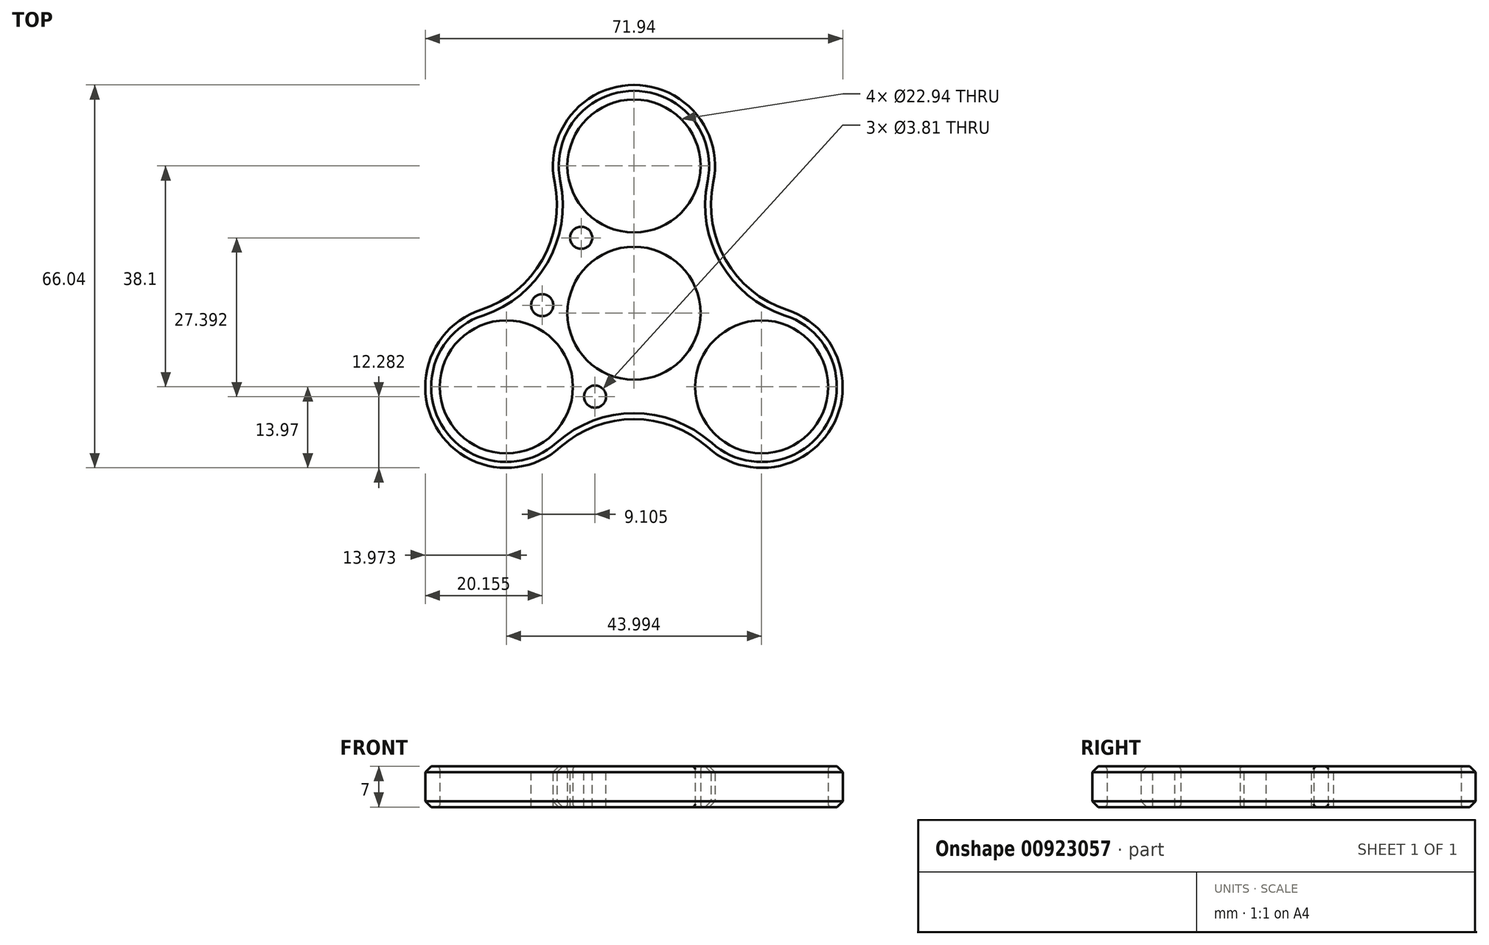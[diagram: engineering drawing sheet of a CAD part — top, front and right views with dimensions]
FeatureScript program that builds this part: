
annotation { "Feature Type Name" : "Feature", "Feature Type Description" : "" }
export const myFeature = defineFeature(function(context is Context, id is Id, definition is map)
    precondition{}
    {
        {
            var Q0;
            Q0=qCreatedBy(makeId("Top.planeOp"),FACE);
            var sketch = newSketch(context, id + "F0", { "sketchPlane" : qUnion([Q0])});
            skCircle(sketch, "E0", {"center": v(0, 0) * mm, "radius": 11.47 * mm});
            skLineSegment(sketch, "E1", {"start": v(0, 0) * mm, "end": v(-51.08, -29.49) * mm});
            skLineSegment(sketch, "E2", {"start": v(0, 0) * mm, "end": v(58.4, -33.72) * mm});
            skCircle(sketch, "E3", {"center": v(0, 25.4) * mm, "radius": 11.47 * mm});
            skCircle(sketch, "E4", {"center": v(22, -12.7) * mm, "radius": 11.47 * mm});
            skCircle(sketch, "E5", {"center": v(-22, -12.7) * mm, "radius": 11.47 * mm});
            skArc(sketch, "E6", {"start": v(12.7, -23.12) * mm, "mid": v(34.1, -19.68) * mm, "end": v(26.37, 0.57) * mm});
            skArc(sketch, "E7", {"start": v(-26.37, 0.57) * mm, "mid": v(-34.1, -19.68) * mm, "end": v(-12.7, -23.12) * mm});
            skArc(sketch, "E8", {"start": v(13.68, 22.55) * mm, "mid": v(0, 39.37) * mm, "end": v(-13.68, 22.55) * mm});
            skArc(sketch, "E9", {"start": v(-26.37, 0.57) * mm, "mid": v(-15.83, 9.14) * mm, "end": v(-13.68, 22.55) * mm});
            skArc(sketch, "E10.1.0", {"start": v(12.7, -23.12) * mm, "mid": v(0, -18.28) * mm, "end": v(-12.7, -23.12) * mm});
            skArc(sketch, "E10.2.0", {"start": v(13.68, 22.55) * mm, "mid": v(15.83, 9.14) * mm, "end": v(26.37, 0.57) * mm});
            skSolve(sketch);
        }
        {
            var Q0;
            Q0=qSketchRegion(id+"F0",true);
            extrude(context, id + "F1", {"entities" : qUnion([Q0]), "depth" : 7 * mm, "offsetDistance" : 25.4 * mm});
        }
        {
            var Q0;
            Q0=makeQuery(id+"F1.opExtrude","CAP_EDGE",EDGE,{"disambiguationData":[OSD([sQuery(id+"F0.wireOp",EDGE,"E5")])],"isStart":false});
            var Q1;
            Q1=makeQuery(id+"F1.opExtrude","CAP_EDGE",EDGE,{"disambiguationData":[OSD([sQuery(id+"F0.wireOp",EDGE,"E4")])],"isStart":false});
            var Q2;
            Q2=makeQuery(id+"F1.opExtrude","CAP_EDGE",EDGE,{"disambiguationData":[OSD([sQuery(id+"F0.wireOp",EDGE,"E3")])],"isStart":false});
            var Q3;
            Q3=makeQuery(id+"F1.opExtrude","CAP_EDGE",EDGE,{"disambiguationData":[OSD([sQuery(id+"F0.wireOp",EDGE,"E0")])],"isStart":false});
            var Q4;
            Q4=makeQuery(id+"F1.opExtrude","CAP_EDGE",EDGE,{"disambiguationData":[OSD([sQuery(id+"F0.wireOp",EDGE,"E5")])],"isStart":true});
            var Q5;
            Q5=makeQuery(id+"F1.opExtrude","CAP_EDGE",EDGE,{"disambiguationData":[OSD([sQuery(id+"F0.wireOp",EDGE,"E3")])],"isStart":true});
            var Q6;
            Q6=makeQuery(id+"F1.opExtrude","CAP_EDGE",EDGE,{"disambiguationData":[OSD([sQuery(id+"F0.wireOp",EDGE,"E0")])],"isStart":true});
            var Q7;
            Q7=makeQuery(id+"F1.opExtrude","CAP_EDGE",EDGE,{"disambiguationData":[OSD([sQuery(id+"F0.wireOp",EDGE,"E4")])],"isStart":true});
            fillet(context, id + "F2", {"entities" : qUnion([Q0, Q1, Q2, Q3, Q4, Q5, Q6, Q7]), "radius" : 0.5 * mm, "tangentPropagation" : true, "allowEdgeOverflow" : false});
        }
        {
            var Q0;
            Q0=makeQuery(id+"F1.opExtrude","CAP_EDGE",EDGE,{"disambiguationData":[OSD([sQuery(id+"F0.wireOp",EDGE,"E9")])],"isStart":false});
            var Q1;
            Q1=makeQuery(id+"F1.opExtrude","CAP_EDGE",EDGE,{"disambiguationData":[OSD([sQuery(id+"F0.wireOp",EDGE,"E9")])],"isStart":true});
            chamfer(context, id + "F3", {"entities" : qUnion([Q0, Q1]), "width" : 1.02 * mm, "tangentPropagation" : true});
        }
        {
            var Q0;
            Q0=makeQuery(id+"F1.opExtrude","CAP_FACE",FACE,{"disambiguationData":[OSD([sQuery(id+"F0.wireOp",EDGE,"E0"),sQuery(id+"F0.wireOp",EDGE,"E3"),sQuery(id+"F0.wireOp",EDGE,"E4"),sQuery(id+"F0.wireOp",EDGE,"E5"),sQuery(id+"F0.wireOp",EDGE,"E6"),sQuery(id+"F0.wireOp",EDGE,"E7"),sQuery(id+"F0.wireOp",EDGE,"E8"),sQuery(id+"F0.wireOp",EDGE,"E9"),sQuery(id+"F0.wireOp",EDGE,"E10.1.0"),sQuery(id+"F0.wireOp",EDGE,"E10.2.0")])],"isStart":false});
            var sketch = newSketch(context, id + "F4", { "sketchPlane" : qUnion([Q0])});
            skCircle(sketch, "E11", {"center": v(-9.1, 13) * mm, "radius": 1.9 * mm});
            skLineSegment(sketch, "E12", {"start": v(0, 0) * mm, "end": v(-27.99, 39.97) * mm, "construction": true});
            skLineSegment(sketch, "E13", {"start": v(0, 0) * mm, "end": v(-37.14, -21.44) * mm, "construction": true});
            skLineSegment(sketch, "E14", {"start": v(0, 0) * mm, "end": v(33.22, -19.18) * mm, "construction": true});
            skCircle(sketch, "E15", {"center": v(-15.81, 1.38) * mm, "radius": 1.9 * mm});
            skLineSegment(sketch, "E16", {"start": v(0, 0) * mm, "end": v(-32.99, 2.89) * mm, "construction": true});
            skCircle(sketch, "E17", {"center": v(-6.7, -14.39) * mm, "radius": 1.9 * mm});
            skLineSegment(sketch, "E18", {"start": v(0, 0) * mm, "end": v(-11.65, -24.97) * mm});
            skSolve(sketch);
        }
        {
            var Q0;
            Q0 = qSketchRegion(id + "F4", true);
            extrude(context, id + "F5", {"entities" : qUnion([Q0]), "operationType" : NewBodyOperationType.REMOVE, "endBound" : BoundingType.THROUGH_ALL, "oppositeDirection" : true, "depth" : 25.4 * mm, "offsetDistance" : 25.4 * mm});
        }
    });
